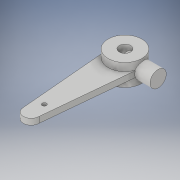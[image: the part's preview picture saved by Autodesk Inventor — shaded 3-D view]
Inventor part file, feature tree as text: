
AUTODESK INVENTOR PART (.ipt)
format: ipt  version: 2018 (Build 220112000, 112)  size: 148,992 bytes
history: native  units: in
note: dims shown in document units (in); Inventor stores cm internally (conversion verified against a paired STEP export)
features: extrude x5, sketch x4, plane x1
ambient origin geometry x8: Origin, YZ Plane, XZ Plane, XY Plane, X Axis, Y Axis, Z Axis, Center Point
bodies: Solid1 (feature_tree)
feature tree (10):
  sketch  "Sketch1"  dims[d0=0.4685in d1=0.2165in]
  extrude  "Extrusion1"  Depth=0.2165in
  extrude  "Extrusion2"  Depth=0.3004in TaperAngle=0.0deg
  extrude  "Extrusion3"  Depth=0.2902in
  extrude  "Extrusion4"  Depth=0.4331in TaperAngle=0.0deg
  plane  "Work Plane1"
  extrude  "Extrusion5"  Depth=0.4331in
  sketch  "Sketch2"  dims[d2=1.302in d3=0.3004in d4=0.0in]
  sketch  "Sketch3"  dims[d5=0.0827in d6=0.0in d7=0.2902in]
  sketch  "Sketch4"  dims[d8=0.0591in d9=0.0827in d10=0.0in d11=0.1575in d12=1.9685in d13=0.0in d14=0.2244in d15=0.4331in d16=0.0in]
